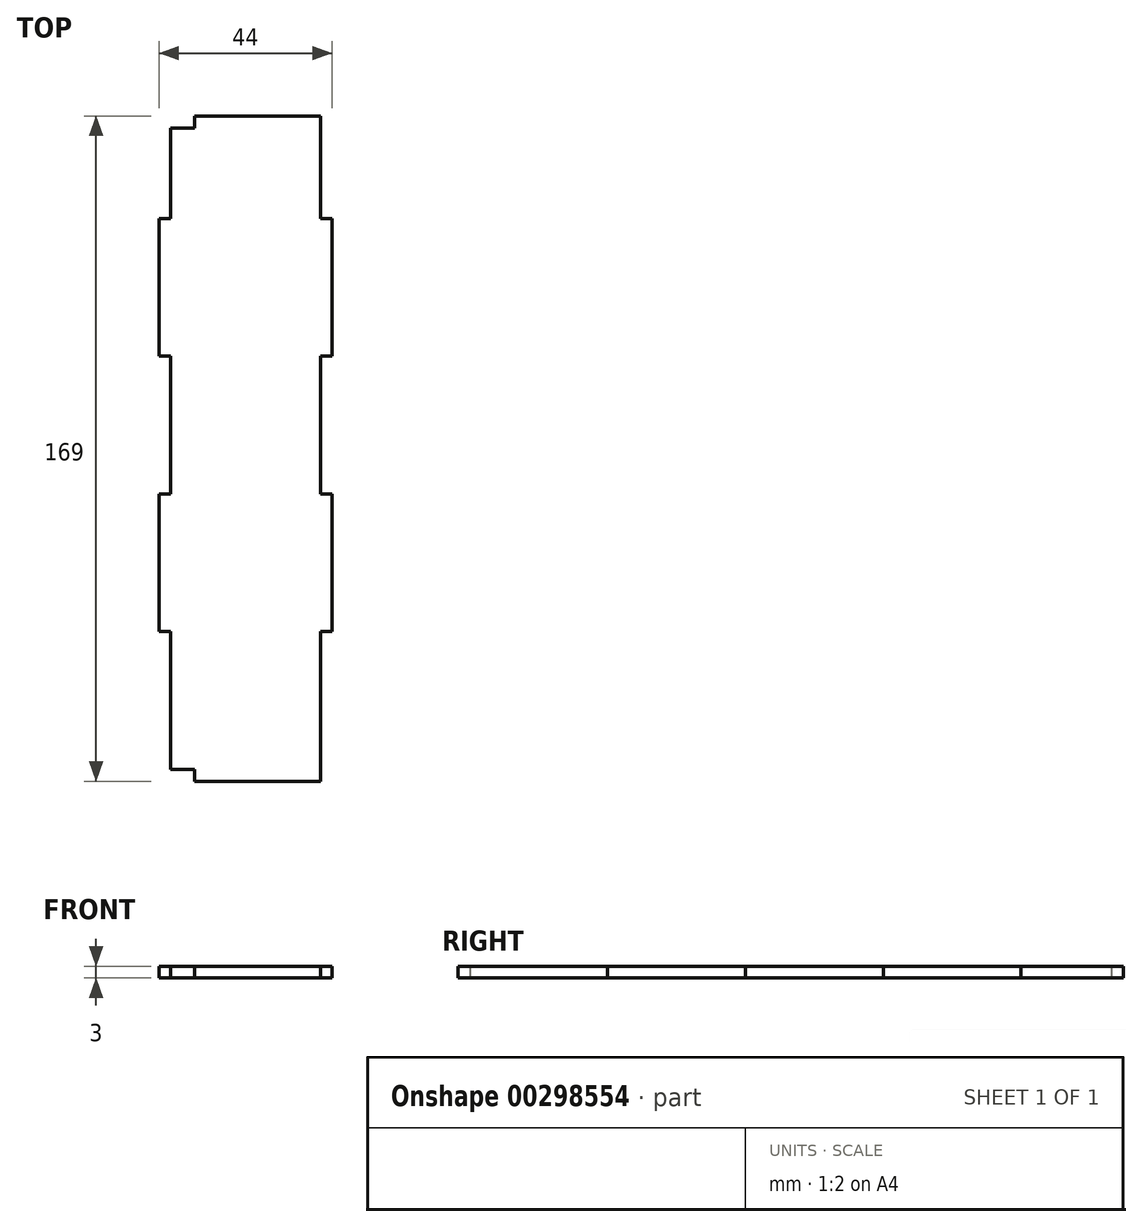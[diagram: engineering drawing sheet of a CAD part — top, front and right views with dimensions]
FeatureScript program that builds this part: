
annotation { "Feature Type Name" : "Feature", "Feature Type Description" : "" }
export const myFeature = defineFeature(function(context is Context, id is Id, definition is map)
    precondition{}
    {
        {
            var Q0;
            Q0=qCreatedBy(makeId("Top.planeOp"),FACE);
            var sketch = newSketch(context, id + "F0", { "sketchPlane" : qUnion([Q0])});
            skPoint(sketch, "E0.middle", {"position": v(0, 0) * mm});
            skLineSegment(sketch, "E1", {"start": v(22, 58.5) * mm, "end": v(22, 23.5) * mm});
            skLineSegment(sketch, "E2", {"start": v(22, -11.5) * mm, "end": v(22, -46.5) * mm});
            skLineSegment(sketch, "E3.top", {"start": v(22, 58.5) * mm, "end": v(19, 58.5) * mm});
            skLineSegment(sketch, "E4.bottom", {"start": v(22, 23.5) * mm, "end": v(19, 23.5) * mm});
            skLineSegment(sketch, "E4.top", {"start": v(22, -11.5) * mm, "end": v(19, -11.5) * mm});
            skLineSegment(sketch, "E5.bottom", {"start": v(22, -46.5) * mm, "end": v(19, -46.5) * mm});
            skLineSegment(sketch, "E5.right", {"start": v(19, -46.5) * mm, "end": v(19, -84.5) * mm});
            skLineSegment(sketch, "E6", {"start": v(19, -84.5) * mm, "end": v(-13, -84.5) * mm});
            skLineSegment(sketch, "E7", {"start": v(-13, -81.5) * mm, "end": v(-13, -84.5) * mm});
            skLineSegment(sketch, "E8.MirrorCS", {"start": v(-22, -11.5) * mm, "end": v(-19, -11.5) * mm});
            skLineSegment(sketch, "E9.MirrorCS", {"start": v(-22, -46.5) * mm, "end": v(-19, -46.5) * mm});
            skLineSegment(sketch, "E10.MirrorCS", {"start": v(-22, 23.5) * mm, "end": v(-19, 23.5) * mm});
            skLineSegment(sketch, "E11.MirrorCS", {"start": v(-22, 58.5) * mm, "end": v(-19, 58.5) * mm});
            skLineSegment(sketch, "E12.MirrorCS", {"start": v(-19, 23.5) * mm, "end": v(-19, -11.5) * mm});
            skLineSegment(sketch, "E13.MirrorCS", {"start": v(-22, -11.5) * mm, "end": v(-22, -46.5) * mm});
            skLineSegment(sketch, "E14.MirrorCS", {"start": v(-22, 58.5) * mm, "end": v(-22, 23.5) * mm});
            skLineSegment(sketch, "E15.top", {"start": v(-19, -81.5) * mm, "end": v(-13, -81.5) * mm});
            skLineSegment(sketch, "E15.left", {"start": v(-19, -46.5) * mm, "end": v(-19, -81.5) * mm});
            skLineSegment(sketch, "E16.MirrorCS", {"start": v(-13, 81.5) * mm, "end": v(-13, 84.5) * mm});
            skLineSegment(sketch, "E17.MirrorCS", {"start": v(19, 84.5) * mm, "end": v(-13, 84.5) * mm});
            skLineSegment(sketch, "E18.MirrorCS", {"start": v(-19, 81.5) * mm, "end": v(-13, 81.5) * mm});
            skLineSegment(sketch, "E19", {"start": v(-19, 81.5) * mm, "end": v(-19, 58.5) * mm});
            skLineSegment(sketch, "E20", {"start": v(19, 84.5) * mm, "end": v(19, 58.5) * mm});
            skLineSegment(sketch, "E21", {"start": v(19, 23.5) * mm, "end": v(19, -11.5) * mm});
            skSolve(sketch);
        }
        {
            var Q0;
            Q0 = qSketchRegion(id + "F0", true);
            extrude(context, id + "F1", {"entities" : qUnion([Q0]), "depth" : 3 * mm});
        }
    });
